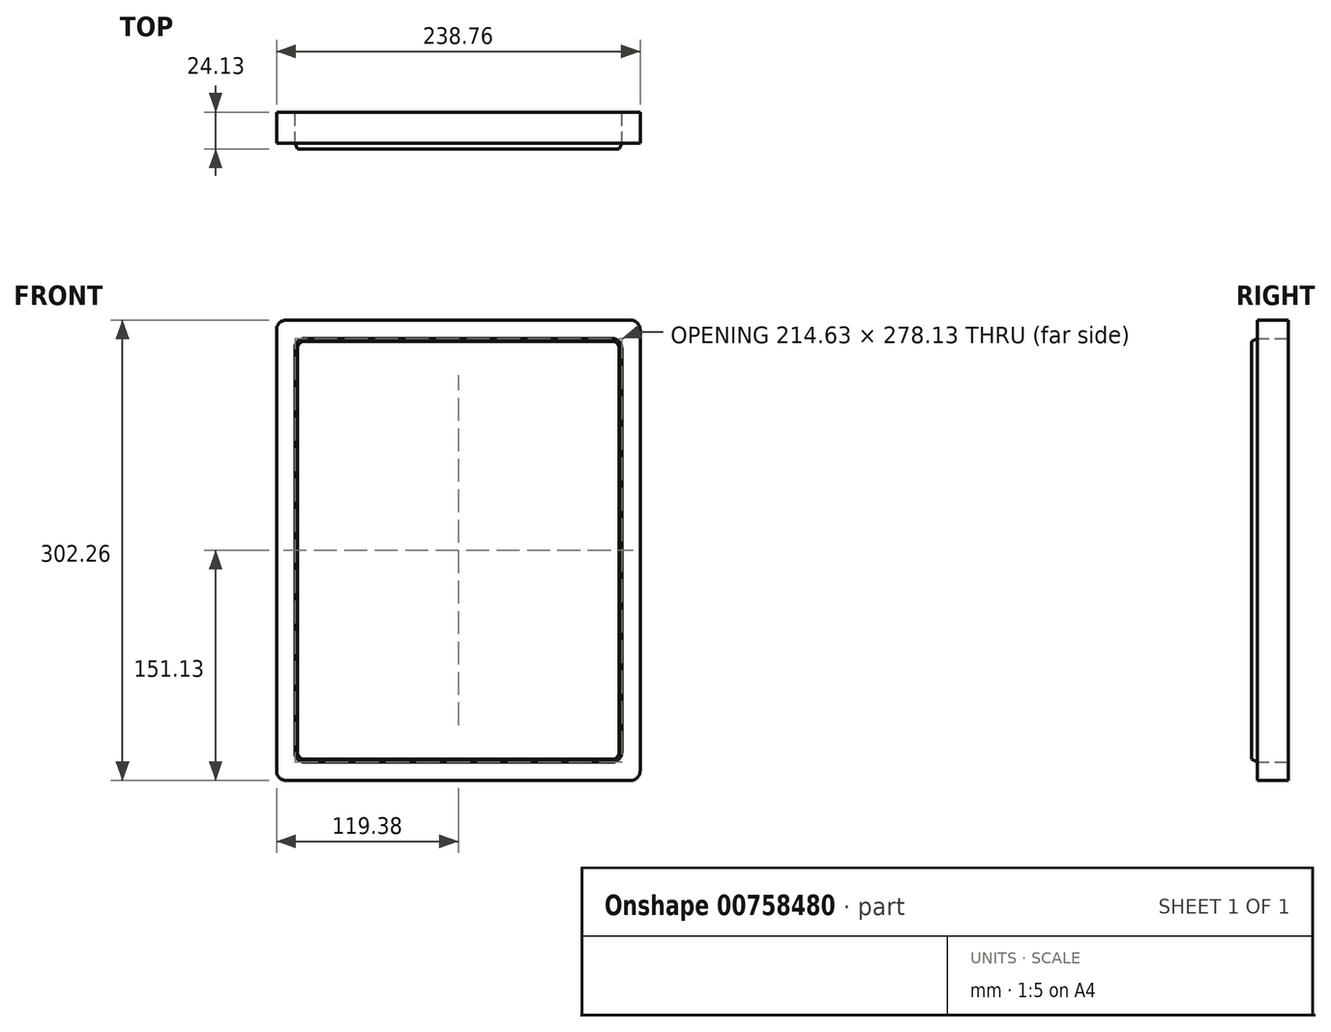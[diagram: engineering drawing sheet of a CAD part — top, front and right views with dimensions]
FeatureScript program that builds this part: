
annotation { "Feature Type Name" : "Feature", "Feature Type Description" : "" }
export const myFeature = defineFeature(function(context is Context, id is Id, definition is map)
    precondition{}
    {
        {
            var Q0;
            Q0=qCreatedBy(makeId("Front.planeOp"),FACE);
            var sketch = newSketch(context, id + "F0", { "sketchPlane" : qUnion([Q0])});
            skLineSegment(sketch, "E0.bottom", {"start": v(100.97, -139.06) * mm, "end": v(-100.97, -139.06) * mm});
            skLineSegment(sketch, "E0.top", {"start": v(100.97, 139.07) * mm, "end": v(-100.97, 139.07) * mm});
            skLineSegment(sketch, "E0.left", {"start": v(107.32, -132.71) * mm, "end": v(107.32, 132.72) * mm});
            skLineSegment(sketch, "E0.right", {"start": v(-107.32, -132.72) * mm, "end": v(-107.31, 132.72) * mm});
            skPoint(sketch, "E0.middle", {"position": v(0, 0) * mm});
            skPoint(sketch, "E1.visualSharp", {"position": v(-107.31, 139.07) * mm});
            skArc(sketch, "E1.filletArc", {"start": v(-100.97, 139.07) * mm, "mid": v(-105.46, 137.2) * mm, "end": v(-107.32, 132.72) * mm});
            skPoint(sketch, "E2.visualSharp", {"position": v(107.32, 139.07) * mm});
            skArc(sketch, "E2.filletArc", {"start": v(107.32, 132.72) * mm, "mid": v(105.46, 137.2) * mm, "end": v(100.97, 139.07) * mm});
            skPoint(sketch, "E3.visualSharp", {"position": v(107.31, -139.06) * mm});
            skArc(sketch, "E3.filletArc", {"start": v(100.97, -139.06) * mm, "mid": v(105.46, -137.2) * mm, "end": v(107.31, -132.71) * mm});
            skPoint(sketch, "E4.visualSharp", {"position": v(-107.32, -139.06) * mm});
            skArc(sketch, "E4.filletArc", {"start": v(-107.32, -132.72) * mm, "mid": v(-105.46, -137.2) * mm, "end": v(-100.97, -139.06) * mm});
            skLineSegment(sketch, "E5.bottom", {"start": v(113.03, -151.13) * mm, "end": v(-113.03, -151.13) * mm});
            skLineSegment(sketch, "E5.top", {"start": v(113.03, 151.13) * mm, "end": v(-113.03, 151.13) * mm});
            skLineSegment(sketch, "E5.left", {"start": v(119.38, -144.78) * mm, "end": v(119.38, 144.78) * mm});
            skLineSegment(sketch, "E5.right", {"start": v(-119.38, -144.78) * mm, "end": v(-119.38, 144.78) * mm});
            skPoint(sketch, "E6.visualSharp", {"position": v(-119.38, 151.13) * mm});
            skArc(sketch, "E6.filletArc", {"start": v(-113.03, 151.13) * mm, "mid": v(-117.52, 149.27) * mm, "end": v(-119.38, 144.78) * mm});
            skPoint(sketch, "E7.visualSharp", {"position": v(119.38, 151.13) * mm});
            skArc(sketch, "E7.filletArc", {"start": v(119.38, 144.78) * mm, "mid": v(117.52, 149.27) * mm, "end": v(113.03, 151.13) * mm});
            skPoint(sketch, "E8.visualSharp", {"position": v(119.38, -151.13) * mm});
            skArc(sketch, "E8.filletArc", {"start": v(113.03, -151.13) * mm, "mid": v(117.52, -149.27) * mm, "end": v(119.38, -144.78) * mm});
            skPoint(sketch, "E9.visualSharp", {"position": v(-119.38, -151.13) * mm});
            skArc(sketch, "E9.filletArc", {"start": v(-119.38, -144.78) * mm, "mid": v(-117.52, -149.27) * mm, "end": v(-113.03, -151.13) * mm});
            skSolve(sketch);
        }
        {
            var Q0;
            Q0=makeQuery(id+"F0.imprint","IMPRINT",FACE,{"disambiguationData":[TD([[makeQuery(id+"F0.imprint","IMPRINT",EDGE,{"derivedFrom":sQuery(id+"F0.wireOp",EDGE,"E0.bottom")}),1.0]])]});
            extrude(context, id + "F1", {"entities" : qUnion([Q0]), "depth" : 20.32 * mm, "offsetDistance" : 25.4 * mm});
        }
        {
            var Q0;
            Q0=makeQuery(id+"F1.opExtrude","CAP_FACE",FACE,{"disambiguationData":[OSD([sQuery(id+"F0.wireOp",EDGE,"E0.bottom"),sQuery(id+"F0.wireOp",EDGE,"E0.top"),sQuery(id+"F0.wireOp",EDGE,"E0.left"),sQuery(id+"F0.wireOp",EDGE,"E0.right"),sQuery(id+"F0.wireOp",EDGE,"E1.filletArc"),sQuery(id+"F0.wireOp",EDGE,"E2.filletArc"),sQuery(id+"F0.wireOp",EDGE,"E3.filletArc"),sQuery(id+"F0.wireOp",EDGE,"E4.filletArc"),sQuery(id+"F0.wireOp",EDGE,"E5.bottom"),sQuery(id+"F0.wireOp",EDGE,"E5.top"),sQuery(id+"F0.wireOp",EDGE,"E5.left"),sQuery(id+"F0.wireOp",EDGE,"E5.right"),sQuery(id+"F0.wireOp",EDGE,"E6.filletArc"),sQuery(id+"F0.wireOp",EDGE,"E7.filletArc"),sQuery(id+"F0.wireOp",EDGE,"E8.filletArc"),sQuery(id+"F0.wireOp",EDGE,"E9.filletArc")])],"isStart":false});
            var sketch = newSketch(context, id + "F2", { "sketchPlane" : qUnion([Q0])});
            skLineSegment(sketch, "E10.bottom", {"start": v(100.96, -139.06) * mm, "end": v(-100.96, -139.06) * mm});
            skLineSegment(sketch, "E10.top", {"start": v(100.96, 139.06) * mm, "end": v(-100.96, 139.06) * mm});
            skLineSegment(sketch, "E10.left", {"start": v(107.31, -132.71) * mm, "end": v(107.31, 132.71) * mm});
            skLineSegment(sketch, "E10.right", {"start": v(-107.31, -132.71) * mm, "end": v(-107.31, 132.71) * mm});
            skPoint(sketch, "E10.middle", {"position": v(0, 0) * mm});
            skPoint(sketch, "E11.visualSharp", {"position": v(107.31, -139.06) * mm});
            skArc(sketch, "E11.filletArc", {"start": v(100.96, -139.06) * mm, "mid": v(105.46, -137.2) * mm, "end": v(107.31, -132.71) * mm});
            skPoint(sketch, "E12.visualSharp", {"position": v(-107.31, -139.06) * mm});
            skArc(sketch, "E12.filletArc", {"start": v(-107.32, -132.71) * mm, "mid": v(-105.46, -137.2) * mm, "end": v(-100.96, -139.06) * mm});
            skPoint(sketch, "E13.visualSharp", {"position": v(-107.31, 139.06) * mm});
            skArc(sketch, "E13.filletArc", {"start": v(-100.96, 139.06) * mm, "mid": v(-105.46, 137.2) * mm, "end": v(-107.31, 132.71) * mm});
            skPoint(sketch, "E14.visualSharp", {"position": v(107.31, 139.06) * mm});
            skArc(sketch, "E14.filletArc", {"start": v(107.31, 132.71) * mm, "mid": v(105.46, 137.2) * mm, "end": v(100.96, 139.06) * mm});
            skSolve(sketch);
        }
        {
            var Q0;
            Q0=makeQuery(id+"F2.imprint","IMPRINT",FACE,{"disambiguationData":[TD([[makeQuery(id+"F2.imprint","IMPRINT",EDGE,{"derivedFrom":sQuery(id+"F2.wireOp",EDGE,"E10.bottom")}),-1.0]])]});
            extrude(context, id + "F3", {"entities" : qUnion([Q0]), "depth" : 3.8 * mm, "offsetDistance" : 25.4 * mm, "hasDraft" : true, "draftAngle" : 25 * degree, "draftPullDirection" : true});
        }
    });
